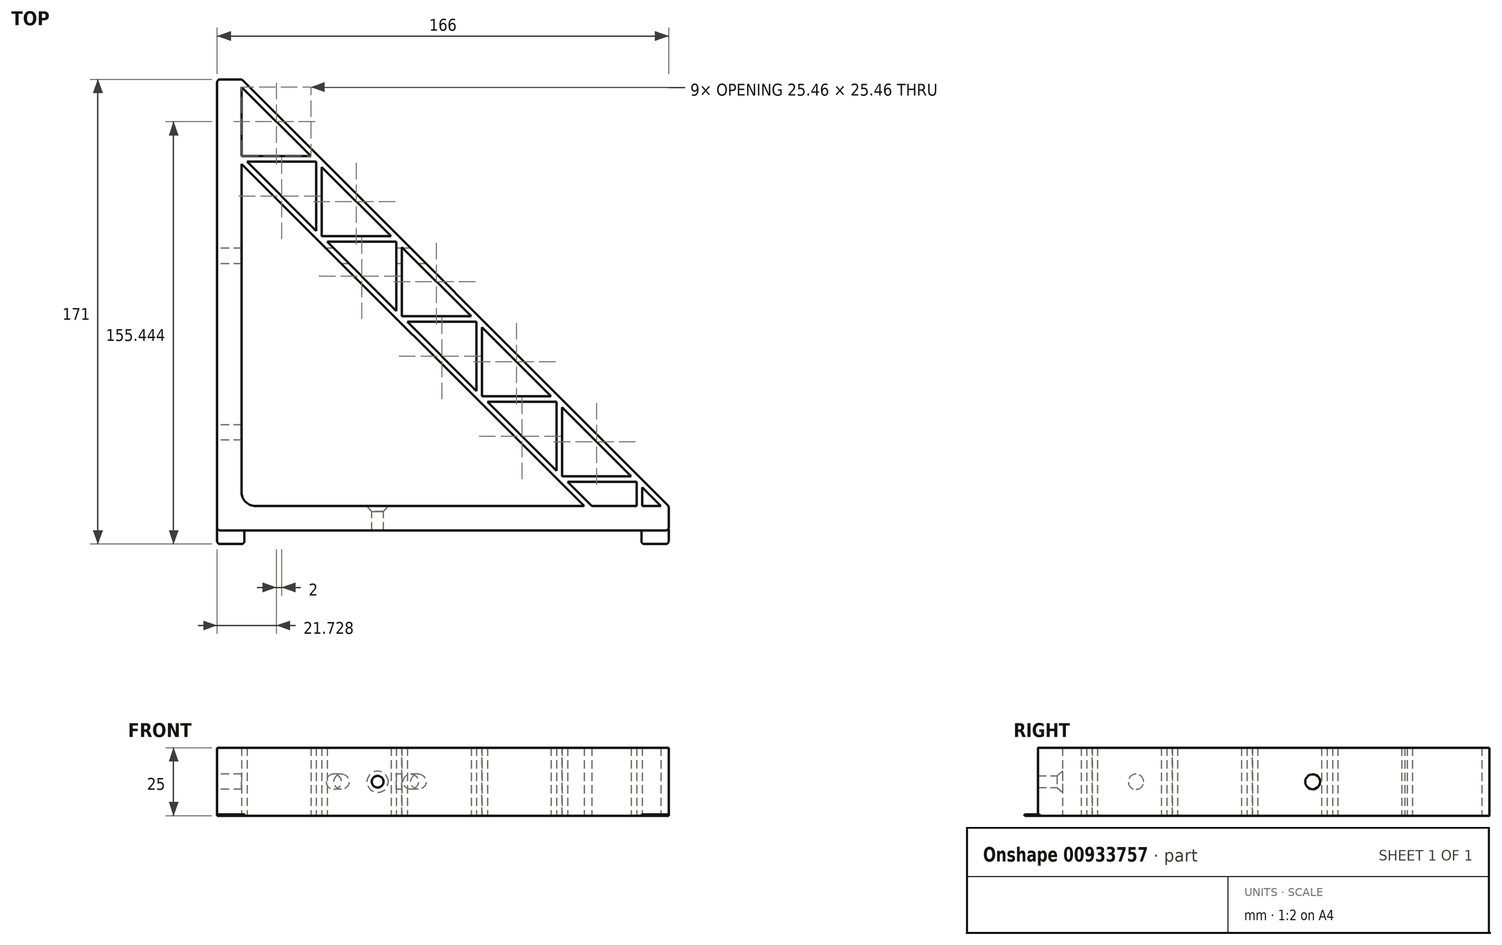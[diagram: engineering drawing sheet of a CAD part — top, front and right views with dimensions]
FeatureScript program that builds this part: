
annotation { "Feature Type Name" : "Feature", "Feature Type Description" : "" }
export const myFeature = defineFeature(function(context is Context, id is Id, definition is map)
    precondition{}
    {
        {
            var Q0;
            Q0=qCreatedBy(makeId("Top.planeOp"),FACE);
            var sketch = newSketch(context, id + "F0", { "sketchPlane" : qUnion([Q0])});
            skLineSegment(sketch, "E0", {"start": v(0, 0) * mm, "end": v(0, 175) * mm});
            skLineSegment(sketch, "E1", {"start": v(0, 175) * mm, "end": v(175, 0) * mm});
            skLineSegment(sketch, "E2", {"start": v(175, 0) * mm, "end": v(0, 0) * mm});
            skLineSegment(sketch, "E3", {"start": v(9, 134.89) * mm, "end": v(9, 9) * mm});
            skLineSegment(sketch, "E4", {"start": v(9, 9) * mm, "end": v(134.89, 9) * mm});
            skLineSegment(sketch, "E5", {"start": v(134.89, 9) * mm, "end": v(9, 134.89) * mm});
            skPoint(sketch, "E6", {"position": v(87.5, 87.5) * mm});
            skPoint(sketch, "E7", {"position": v(71.94, 71.94) * mm});
            skLineSegment(sketch, "E8", {"start": v(9, 163.17) * mm, "end": v(9, 137.72) * mm});
            skLineSegment(sketch, "E9", {"start": v(9, 137.72) * mm, "end": v(34.46, 137.72) * mm});
            skLineSegment(sketch, "E10", {"start": v(11, 135.72) * mm, "end": v(36.46, 135.72) * mm});
            skPoint(sketch, "E11", {"position": v(23.73, 135.72) * mm});
            skLineSegment(sketch, "E12", {"start": v(36.46, 135.72) * mm, "end": v(36.46, 110.26) * mm});
            skLineSegment(sketch, "E13", {"start": v(38.46, 108.26) * mm, "end": v(38.46, 133.72) * mm});
            skLineSegment(sketch, "E14", {"start": v(134.89, 9) * mm, "end": v(166, 9) * mm});
            skLineSegment(sketch, "E15", {"start": v(9, 134.89) * mm, "end": v(9, 138.17) * mm});
            skPoint(sketch, "E16", {"position": v(137.72, 9) * mm});
            skLineSegment(sketch, "E17", {"start": v(9, 137.72) * mm, "end": v(137.72, 9) * mm});
            skPoint(sketch, "E18", {"position": v(150.27, 21.9) * mm});
            skLineSegment(sketch, "E19", {"start": v(9, 163.17) * mm, "end": v(150.27, 21.9) * mm});
            skLineSegment(sketch, "E20", {"start": v(166, 9) * mm, "end": v(166, 0) * mm});
            skLineSegment(sketch, "E21", {"start": v(9, 163.17) * mm, "end": v(9, 166) * mm});
            skLineSegment(sketch, "E22", {"start": v(9, 166) * mm, "end": v(0, 166) * mm});
            skLineSegment(sketch, "E23.1.0.0", {"start": v(38.46, 108.26) * mm, "end": v(63.91, 108.26) * mm});
            skLineSegment(sketch, "E23.1.0.1", {"start": v(40.46, 106.26) * mm, "end": v(65.91, 106.26) * mm});
            skLineSegment(sketch, "E23.1.0.2", {"start": v(65.91, 106.26) * mm, "end": v(65.91, 80.8) * mm});
            skLineSegment(sketch, "E23.1.0.3", {"start": v(67.91, 78.8) * mm, "end": v(67.91, 104.26) * mm});
            skLineSegment(sketch, "E23.2.0.0", {"start": v(67.91, 78.8) * mm, "end": v(93.37, 78.8) * mm});
            skLineSegment(sketch, "E23.2.0.1", {"start": v(69.91, 76.8) * mm, "end": v(95.37, 76.8) * mm});
            skLineSegment(sketch, "E23.2.0.2", {"start": v(95.37, 76.8) * mm, "end": v(95.37, 51.35) * mm});
            skLineSegment(sketch, "E23.2.0.3", {"start": v(97.37, 49.35) * mm, "end": v(97.37, 74.8) * mm});
            skLineSegment(sketch, "E23.direction1", {"start": v(9, 137.72) * mm, "end": v(38.46, 108.26) * mm, "construction": true});
            skLineSegment(sketch, "E24.0.3.0", {"start": v(97.37, 49.35) * mm, "end": v(122.82, 49.35) * mm});
            skLineSegment(sketch, "E24.3.3.0", {"start": v(99.37, 47.35) * mm, "end": v(124.82, 47.35) * mm});
            skLineSegment(sketch, "E24.6.3.0", {"start": v(124.82, 47.35) * mm, "end": v(124.82, 21.9) * mm});
            skLineSegment(sketch, "E24.9.3.0", {"start": v(126.82, 19.9) * mm, "end": v(126.82, 45.35) * mm});
            skLineSegment(sketch, "E24.0.4.0", {"start": v(126.82, 19.9) * mm, "end": v(152.28, 19.9) * mm});
            skLineSegment(sketch, "E24.3.4.0", {"start": v(128.82, 17.9) * mm, "end": v(154.28, 17.9) * mm});
            skLineSegment(sketch, "E24.6.4.0", {"start": v(154.28, 17.9) * mm, "end": v(154.28, -7.56) * mm});
            skLineSegment(sketch, "E24.9.4.0", {"start": v(156.28, -9.56) * mm, "end": v(156.28, 15.9) * mm});
            skLineSegment(sketch, "E25", {"start": v(150.27, 21.9) * mm, "end": v(172.17, 0) * mm});
            skSolve(sketch);
        }
        {
            var Q0;
            Q0=makeQuery(id+"F0.imprint","IMPRINT",FACE,{"disambiguationData":[TD([[makeQuery(id+"F0.imprint","IMPRINT",EDGE,{"derivedFrom":sQuery(id+"F0.wireOp",EDGE,"E3")}),-1.0]])]});
            var Q1;
            {var subQ5=sQuery(id+"F0.wireOp",EDGE,"E8");Q1=makeQuery(id+"F0.imprint","IMPRINT",FACE,{"disambiguationData":[TD([[makeQuery(id+"F0.imprint","IMPRINT",EDGE,{"derivedFrom":subQ5}),-1.0]])]});}
            var Q2;
            {var subQ0=sQuery(id+"F0.wireOp",EDGE,"E9");Q2=makeQuery(id+"F0.imprint","IMPRINT",FACE,{"disambiguationData":[TD([[makeQuery(id+"F0.imprint","IMPRINT",EDGE,{"derivedFrom":subQ0}),-1.0]])]});}
            var Q3;
            {var subQ0=sQuery(id+"F0.wireOp",EDGE,"E12");Q3=makeQuery(id+"F0.imprint","IMPRINT",FACE,{"disambiguationData":[TD([[makeQuery(id+"F0.imprint","IMPRINT",EDGE,{"derivedFrom":subQ0}),1.0]])]});}
            var Q4;
            {var subQ0=sQuery(id+"F0.wireOp",EDGE,"t3oYEMUN-sFDN-Q4uO-rre0-XmO0z3MUqwwg");Q4=makeQuery(id+"F0.imprint","IMPRINT",FACE,{"disambiguationData":[TD([[makeQuery(id+"F0.imprint","IMPRINT",EDGE,{"derivedFrom":subQ0}),-1.0]])]});}
            var Q5;
            {var subQ0=sQuery(id+"F0.wireOp",EDGE,"Gh5ZCY8b-JTnj-C4Vn-PBZv-iaPauiYJcpUC");Q5=makeQuery(id+"F0.imprint","IMPRINT",FACE,{"disambiguationData":[TD([[makeQuery(id+"F0.imprint","IMPRINT",EDGE,{"derivedFrom":subQ0}),1.0]])]});}
            var Q6;
            {var subQ0=sQuery(id+"F0.wireOp",EDGE,"uzZHcgCa-ZNne-41at-UcpQ-2XL1grKBjjWO");Q6=makeQuery(id+"F0.imprint","IMPRINT",FACE,{"disambiguationData":[TD([[makeQuery(id+"F0.imprint","IMPRINT",EDGE,{"derivedFrom":subQ0}),-1.0]])]});}
            var Q7;
            {var subQ0=sQuery(id+"F0.wireOp",EDGE,"vpBYavAs-v1ow-tuZv-KXIh-prGS5gAtpX7B");Q7=makeQuery(id+"F0.imprint","IMPRINT",FACE,{"disambiguationData":[TD([[makeQuery(id+"F0.imprint","IMPRINT",EDGE,{"derivedFrom":subQ0}),1.0]])]});}
            var Q8;
            {var subQ0=sQuery(id+"F0.wireOp",EDGE,"fNY8aZDA-NZx5-W13j-vITE-4YfcdmMxDZ5e");Q8=makeQuery(id+"F0.imprint","IMPRINT",FACE,{"disambiguationData":[TD([[makeQuery(id+"F0.imprint","IMPRINT",EDGE,{"derivedFrom":subQ0}),-1.0]])]});}
            var Q9;
            {var subQ0=sQuery(id+"F0.wireOp",EDGE,"PBqfKtz1-XXqo-IEwp-yejb-xkakkozYTLbb");Q9=makeQuery(id+"F0.imprint","IMPRINT",FACE,{"disambiguationData":[TD([[makeQuery(id+"F0.imprint","IMPRINT",EDGE,{"derivedFrom":subQ0}),1.0]])]});}
            var Q10;
            {var subQ0=sQuery(id+"F0.wireOp",EDGE,"PBqfKtz1-XXqo-IEwp-yejb-xkakkozYTLbb");var subQ1=sQuery(id+"F0.wireOp",EDGE,"0tnvtRqo-Ka0R-me24-QFtn-nfTgzuCr438E");var subQ2=makeQuery(id+"F0.imprint","INTERSECT",VERTEX,{"derivedFrom":[subQ1,subQ0]});Q10=makeQuery(id+"F0.imprint","IMPRINT",FACE,{"disambiguationData":[TD([[makeQuery(id+"F0.imprint","IMPRINT",EDGE,{"disambiguationData":[TD([[subQ2,1.0]])],"derivedFrom":subQ1}),1.0]])]});}
            var Q11;
            {var subQ1=sQuery(id+"F0.wireOp",EDGE,"TcHh0TCD-bz2r-2cmx-PJUQ-hrZb60m40xgq");var subQ5=sQuery(id+"F0.wireOp",EDGE,"0tnvtRqo-Ka0R-me24-QFtn-nfTgzuCr438E");var subQ6=makeQuery(id+"F0.imprint","INTERSECT",VERTEX,{"derivedFrom":[subQ5,subQ1]});Q11=makeQuery(id+"F0.imprint","IMPRINT",FACE,{"disambiguationData":[TD([[makeQuery(id+"F0.imprint","IMPRINT",EDGE,{"disambiguationData":[TD([[subQ6,1.0]])],"derivedFrom":subQ5}),1.0]])]});}
            var Q12;
            {var subQ0=sQuery(id+"F0.wireOp",EDGE,"TcHh0TCD-bz2r-2cmx-PJUQ-hrZb60m40xgq");var subQ1=sQuery(id+"F0.wireOp",EDGE,"p0dbSUAr-ZKRw-19DJ-W5tp-fSP5nnLVepNG");var subQ2=makeQuery(id+"F0.imprint","INTERSECT",VERTEX,{"derivedFrom":[subQ1,subQ0]});Q12=makeQuery(id+"F0.imprint","IMPRINT",FACE,{"disambiguationData":[TD([[makeQuery(id+"F0.imprint","IMPRINT",EDGE,{"disambiguationData":[TD([[subQ2,-1.0]])],"derivedFrom":subQ1}),1.0]])]});}
            var Q13;
            {var subQ0=sQuery(id+"F0.wireOp",EDGE,"E10");var subQ1=sQuery(id+"F0.wireOp",EDGE,"0tnvtRqo-Ka0R-me24-QFtn-nfTgzuCr438E");var subQ2=makeQuery(id+"F0.imprint","INTERSECT",VERTEX,{"derivedFrom":[subQ1,subQ0]});Q13=makeQuery(id+"F0.imprint","IMPRINT",FACE,{"disambiguationData":[TD([[makeQuery(id+"F0.imprint","IMPRINT",EDGE,{"disambiguationData":[TD([[subQ2,-1.0]])],"derivedFrom":subQ1}),1.0]])]});}
            var Q14;
            {var subQ11=sQuery(id+"F0.wireOp",EDGE,"E5");Q14=makeQuery(id+"F0.imprint","IMPRINT",FACE,{"disambiguationData":[TD([[makeQuery(id+"F0.imprint","IMPRINT",EDGE,{"derivedFrom":subQ11}),-1.0]])]});}
            var Q15;
            {var subQ0=sQuery(id+"F0.wireOp",EDGE,"3CZCHI8V-pq78-QH3n-k3AF-cjWYhrhBDTe4");Q15=makeQuery(id+"F0.imprint","IMPRINT",FACE,{"disambiguationData":[TD([[makeQuery(id+"F0.imprint","IMPRINT",EDGE,{"derivedFrom":subQ0}),-1.0]])]});}
            var Q16;
            {var subQ7=sQuery(id+"F0.wireOp",EDGE,"E21");Q16=makeQuery(id+"F0.imprint","IMPRINT",FACE,{"disambiguationData":[TD([[makeQuery(id+"F0.imprint","IMPRINT",EDGE,{"derivedFrom":subQ7}),-1.0]])]});}
            var Q17;
            {var subQ0=sQuery(id+"F0.wireOp",EDGE,"E23.1.0.0");Q17=makeQuery(id+"F0.imprint","IMPRINT",FACE,{"disambiguationData":[TD([[makeQuery(id+"F0.imprint","IMPRINT",EDGE,{"derivedFrom":subQ0}),-1.0]])]});}
            var Q18;
            {var subQ0=sQuery(id+"F0.wireOp",EDGE,"E23.1.0.2");Q18=makeQuery(id+"F0.imprint","IMPRINT",FACE,{"disambiguationData":[TD([[makeQuery(id+"F0.imprint","IMPRINT",EDGE,{"derivedFrom":subQ0}),1.0]])]});}
            var Q19;
            {var subQ0=sQuery(id+"F0.wireOp",EDGE,"E23.2.0.0");Q19=makeQuery(id+"F0.imprint","IMPRINT",FACE,{"disambiguationData":[TD([[makeQuery(id+"F0.imprint","IMPRINT",EDGE,{"derivedFrom":subQ0}),-1.0]])]});}
            var Q20;
            {var subQ0=sQuery(id+"F0.wireOp",EDGE,"E23.2.0.2");Q20=makeQuery(id+"F0.imprint","IMPRINT",FACE,{"disambiguationData":[TD([[makeQuery(id+"F0.imprint","IMPRINT",EDGE,{"derivedFrom":subQ0}),1.0]])]});}
            var Q21;
            {var subQ0=sQuery(id+"F0.wireOp",EDGE,"E24.0.3.0");Q21=makeQuery(id+"F0.imprint","IMPRINT",FACE,{"disambiguationData":[TD([[makeQuery(id+"F0.imprint","IMPRINT",EDGE,{"derivedFrom":subQ0}),-1.0]])]});}
            var Q22;
            {var subQ0=sQuery(id+"F0.wireOp",EDGE,"E24.6.3.0");Q22=makeQuery(id+"F0.imprint","IMPRINT",FACE,{"disambiguationData":[TD([[makeQuery(id+"F0.imprint","IMPRINT",EDGE,{"derivedFrom":subQ0}),1.0]])]});}
            var Q23;
            {var subQ0=sQuery(id+"F0.wireOp",EDGE,"E24.0.4.0");Q23=makeQuery(id+"F0.imprint","IMPRINT",FACE,{"disambiguationData":[TD([[makeQuery(id+"F0.imprint","IMPRINT",EDGE,{"derivedFrom":subQ0}),-1.0]])]});}
            var Q24;
            {var subQ0=sQuery(id+"F0.wireOp",EDGE,"E24.6.4.0");var subQ1=sQuery(id+"F0.wireOp",EDGE,"E14");var subQ2=makeQuery(id+"F0.imprint","INTERSECT",VERTEX,{"derivedFrom":[subQ1,subQ0]});Q24=makeQuery(id+"F0.imprint","IMPRINT",FACE,{"disambiguationData":[TD([[makeQuery(id+"F0.imprint","IMPRINT",EDGE,{"disambiguationData":[TD([[subQ2,-1.0]])],"derivedFrom":subQ1}),1.0]])]});}
            var Q25;
            {var subQ0=sQuery(id+"F0.wireOp",EDGE,"E24.9.4.0");var subQ1=sQuery(id+"F0.wireOp",EDGE,"E2");var subQ2=makeQuery(id+"F0.imprint","INTERSECT",VERTEX,{"derivedFrom":[subQ1,subQ0]});Q25=makeQuery(id+"F0.imprint","IMPRINT",FACE,{"disambiguationData":[TD([[makeQuery(id+"F0.imprint","IMPRINT",EDGE,{"disambiguationData":[TD([[subQ2,-1.0]])],"derivedFrom":subQ1}),-1.0]])]});}
            var Q26;
            {var subQ0=sQuery(id+"F0.wireOp",EDGE,"E20");var subQ1=sQuery(id+"F0.wireOp",EDGE,"E2");var subQ2=makeQuery(id+"F0.imprint","INTERSECT",VERTEX,{"derivedFrom":[subQ1,subQ0]});Q26=makeQuery(id+"F0.imprint","IMPRINT",FACE,{"disambiguationData":[TD([[makeQuery(id+"F0.imprint","IMPRINT",EDGE,{"disambiguationData":[TD([[subQ2,-1.0]])],"derivedFrom":subQ1}),-1.0]])]});}
            var Q27;
            {var subQ1=sQuery(id+"F0.wireOp",EDGE,"E14");var subQ3=sQuery(id+"F0.wireOp",EDGE,"E25");var subQ4=makeQuery(id+"F0.imprint","INTERSECT",VERTEX,{"derivedFrom":[subQ1,subQ3]});Q27=makeQuery(id+"F0.imprint","IMPRINT",FACE,{"disambiguationData":[TD([[makeQuery(id+"F0.imprint","IMPRINT",EDGE,{"disambiguationData":[TD([[subQ4,-1.0]])],"derivedFrom":subQ3}),1.0]])]});}
            extrude(context, id + "F1", {"entities" : qUnion([Q0, Q1, Q2, Q3, Q4, Q5, Q6, Q7, Q8, Q9, Q10, Q11, Q12, Q13, Q14, Q15, Q16, Q17, Q18, Q19, Q20, Q21, Q22, Q23, Q24, Q25, Q26, Q27]), "depth" : 25 * mm, "offsetDistance" : 25 * mm});
        }
        {
            var Q0;
            Q0=makeQuery(id+"F1.opExtrude","SWEPT_FACE",FACE,{"disambiguationData":[OSD([sQuery(id+"F0.wireOp",EDGE,"E0")])]});
            var sketch = newSketch(context, id + "F2", { "sketchPlane" : qUnion([Q0])});
            skLineSegment(sketch, "E26", {"start": v(0, 12.5) * mm, "end": v(-166, 12.5) * mm, "construction": true});
            skLineSegment(sketch, "E27", {"start": v(-9, 25) * mm, "end": v(-9, 0) * mm, "construction": true});
            skPoint(sketch, "E28", {"position": v(-9, 12.5) * mm});
            skPoint(sketch, "E29", {"position": v(-36, 12.5) * mm});
            skPoint(sketch, "E30", {"position": v(-86, 12.5) * mm});
            skSolve(sketch);
        }
        {
            var Q0;
            Q0=sQuery(id+"F2.wireOp",VERTEX,"E29");
            var Q1;
            Q1=makeQuery(id+"F1.opExtrude","SWEPT_BODY",BODY,{"disambiguationData":[OSD([sQuery(id+"F0.wireOp",EDGE,"E0"),sQuery(id+"F0.wireOp",EDGE,"E1"),sQuery(id+"F0.wireOp",EDGE,"E2"),sQuery(id+"F0.wireOp",EDGE,"E3"),sQuery(id+"F0.wireOp",EDGE,"E4"),sQuery(id+"F0.wireOp",EDGE,"E5"),sQuery(id+"F0.wireOp",EDGE,"E9"),sQuery(id+"F0.wireOp",EDGE,"E10"),sQuery(id+"F0.wireOp",EDGE,"E12"),sQuery(id+"F0.wireOp",EDGE,"E13"),sQuery(id+"F0.wireOp",EDGE,"t3oYEMUN-sFDN-Q4uO-rre0-XmO0z3MUqwwg"),sQuery(id+"F0.wireOp",EDGE,"wbD9qHZu-pqNc-cMZF-pwQb-4rQk1D1zuLdl"),sQuery(id+"F0.wireOp",EDGE,"Gh5ZCY8b-JTnj-C4Vn-PBZv-iaPauiYJcpUC"),sQuery(id+"F0.wireOp",EDGE,"IqIC1HOr-2qrz-Gsiv-DJaI-mmAGYpswksB0"),sQuery(id+"F0.wireOp",EDGE,"uzZHcgCa-ZNne-41at-UcpQ-2XL1grKBjjWO"),sQuery(id+"F0.wireOp",EDGE,"U4Ez3DGl-Xapn-CNsW-HCYy-rBAmkq0lTpTK"),sQuery(id+"F0.wireOp",EDGE,"vpBYavAs-v1ow-tuZv-KXIh-prGS5gAtpX7B"),sQuery(id+"F0.wireOp",EDGE,"AZhl3Uul-uOOh-n7bd-IfFj-a6V9GQ91CMK2"),sQuery(id+"F0.wireOp",EDGE,"fNY8aZDA-NZx5-W13j-vITE-4YfcdmMxDZ5e"),sQuery(id+"F0.wireOp",EDGE,"W6oHj5A9-C86R-qUiH-kgSU-SLB568lxmBaT"),sQuery(id+"F0.wireOp",EDGE,"3CZCHI8V-pq78-QH3n-k3AF-cjWYhrhBDTe4"),sQuery(id+"F0.wireOp",EDGE,"E14"),sQuery(id+"F0.wireOp",EDGE,"E15"),sQuery(id+"F0.wireOp",EDGE,"rwknU0Rr-BnYf-MzcB-lmkz-0eZFg8cNU43Z"),sQuery(id+"F0.wireOp",EDGE,"E17"),sQuery(id+"F0.wireOp",EDGE,"E19")])]});
            hole(context, id + "F3", {"style" : HoleStyle.SIMPLE, "endStyle" : HoleEndStyle.BLIND, "standardTappedOrClearance" : lookupTablePath({ "fit" : "Normal (ASME)", "standard" : "ANSI", "size" : "#10", "type" : "Clearance" }), "standardBlindInLast" : lookupTablePath({ "fit" : "Normal", "standard" : "ANSI", "engagement" : "75%", "pitch" : "24 tpi", "size" : "#10", "type" : "Clearance & tapped" }), "holeDiameter" : 5.61 * mm, "majorDiameter" : 5 * mm, "holeDepth" : 25 * mm, "isTappedThrough" : true, "tappedDepth" : 12 * mm, "tapClearance" : 3, "locations" : qUnion([Q0]), "scope" : qUnion([Q1])});
        }
        {
            var Q0;
            Q0=makeQuery(id+"F1.opExtrude","SWEPT_FACE",FACE,{"disambiguationData":[OSD([sQuery(id+"F0.wireOp",EDGE,"E0")])]});
            var sketch = newSketch(context, id + "F4", { "sketchPlane" : qUnion([Q0])});
            skLineSegment(sketch, "E31", {"start": v(0, 12.5) * mm, "end": v(-166, 12.5) * mm, "construction": true});
            skPoint(sketch, "E32", {"position": v(-36, 12.5) * mm});
            skPoint(sketch, "E33", {"position": v(-101, 12.5) * mm});
            skSolve(sketch);
        }
        {
            var Q0;
            Q0=sQuery(id+"F4.wireOp",VERTEX,"E33");
            var Q1;
            Q1=makeQuery(id+"F1.opExtrude","SWEPT_BODY",BODY,{"disambiguationData":[OSD([sQuery(id+"F0.wireOp",EDGE,"E0"),sQuery(id+"F0.wireOp",EDGE,"E1"),sQuery(id+"F0.wireOp",EDGE,"E2"),sQuery(id+"F0.wireOp",EDGE,"E3"),sQuery(id+"F0.wireOp",EDGE,"E4"),sQuery(id+"F0.wireOp",EDGE,"E5"),sQuery(id+"F0.wireOp",EDGE,"E9"),sQuery(id+"F0.wireOp",EDGE,"E10"),sQuery(id+"F0.wireOp",EDGE,"E12"),sQuery(id+"F0.wireOp",EDGE,"E13"),sQuery(id+"F0.wireOp",EDGE,"t3oYEMUN-sFDN-Q4uO-rre0-XmO0z3MUqwwg"),sQuery(id+"F0.wireOp",EDGE,"wbD9qHZu-pqNc-cMZF-pwQb-4rQk1D1zuLdl"),sQuery(id+"F0.wireOp",EDGE,"Gh5ZCY8b-JTnj-C4Vn-PBZv-iaPauiYJcpUC"),sQuery(id+"F0.wireOp",EDGE,"IqIC1HOr-2qrz-Gsiv-DJaI-mmAGYpswksB0"),sQuery(id+"F0.wireOp",EDGE,"uzZHcgCa-ZNne-41at-UcpQ-2XL1grKBjjWO"),sQuery(id+"F0.wireOp",EDGE,"U4Ez3DGl-Xapn-CNsW-HCYy-rBAmkq0lTpTK"),sQuery(id+"F0.wireOp",EDGE,"vpBYavAs-v1ow-tuZv-KXIh-prGS5gAtpX7B"),sQuery(id+"F0.wireOp",EDGE,"AZhl3Uul-uOOh-n7bd-IfFj-a6V9GQ91CMK2"),sQuery(id+"F0.wireOp",EDGE,"fNY8aZDA-NZx5-W13j-vITE-4YfcdmMxDZ5e"),sQuery(id+"F0.wireOp",EDGE,"W6oHj5A9-C86R-qUiH-kgSU-SLB568lxmBaT"),sQuery(id+"F0.wireOp",EDGE,"3CZCHI8V-pq78-QH3n-k3AF-cjWYhrhBDTe4"),sQuery(id+"F0.wireOp",EDGE,"E14"),sQuery(id+"F0.wireOp",EDGE,"E15"),sQuery(id+"F0.wireOp",EDGE,"rwknU0Rr-BnYf-MzcB-lmkz-0eZFg8cNU43Z"),sQuery(id+"F0.wireOp",EDGE,"E17"),sQuery(id+"F0.wireOp",EDGE,"E19")])]});
            hole(context, id + "F5", {"style" : HoleStyle.SIMPLE, "endStyle" : HoleEndStyle.BLIND, "standardTappedOrClearance" : lookupTablePath({ "fit" : "Normal (ASME)", "standard" : "ANSI", "size" : "#10", "type" : "Clearance" }), "standardBlindInLast" : lookupTablePath({ "fit" : "Normal", "standard" : "ANSI", "engagement" : "75%", "pitch" : "24 tpi", "size" : "#10", "type" : "Clearance & tapped" }), "holeDiameter" : 5.61 * mm, "majorDiameter" : 5 * mm, "holeDepth" : 85 * mm, "isTappedThrough" : true, "tappedDepth" : 12 * mm, "tapClearance" : 3, "locations" : qUnion([Q0]), "scope" : qUnion([Q1])});
        }
        {
            var Q0;
            Q0=makeQuery(id+"F1.opExtrude","SWEPT_FACE",FACE,{"disambiguationData":[OSD([sQuery(id+"F0.wireOp",EDGE,"E4")])]});
            var sketch = newSketch(context, id + "F6", { "sketchPlane" : qUnion([Q0])});
            skLineSegment(sketch, "E34", {"start": v(-9, 12.5) * mm, "end": v(-59.86, 12.5) * mm, "construction": true});
            skPoint(sketch, "E35", {"position": v(-59, 12.5) * mm});
            skSolve(sketch);
        }
        {
            var Q0;
            Q0=sQuery(id+"F6.wireOp",VERTEX,"E35");
            var Q1;
            Q1=makeQuery(id+"F1.opExtrude","SWEPT_BODY",BODY,{"disambiguationData":[OSD([sQuery(id+"F0.wireOp",EDGE,"E0"),sQuery(id+"F0.wireOp",EDGE,"E1"),sQuery(id+"F0.wireOp",EDGE,"E2"),sQuery(id+"F0.wireOp",EDGE,"E3"),sQuery(id+"F0.wireOp",EDGE,"E4"),sQuery(id+"F0.wireOp",EDGE,"E5"),sQuery(id+"F0.wireOp",EDGE,"E9"),sQuery(id+"F0.wireOp",EDGE,"E10"),sQuery(id+"F0.wireOp",EDGE,"E12"),sQuery(id+"F0.wireOp",EDGE,"E13"),sQuery(id+"F0.wireOp",EDGE,"t3oYEMUN-sFDN-Q4uO-rre0-XmO0z3MUqwwg"),sQuery(id+"F0.wireOp",EDGE,"wbD9qHZu-pqNc-cMZF-pwQb-4rQk1D1zuLdl"),sQuery(id+"F0.wireOp",EDGE,"Gh5ZCY8b-JTnj-C4Vn-PBZv-iaPauiYJcpUC"),sQuery(id+"F0.wireOp",EDGE,"IqIC1HOr-2qrz-Gsiv-DJaI-mmAGYpswksB0"),sQuery(id+"F0.wireOp",EDGE,"uzZHcgCa-ZNne-41at-UcpQ-2XL1grKBjjWO"),sQuery(id+"F0.wireOp",EDGE,"U4Ez3DGl-Xapn-CNsW-HCYy-rBAmkq0lTpTK"),sQuery(id+"F0.wireOp",EDGE,"vpBYavAs-v1ow-tuZv-KXIh-prGS5gAtpX7B"),sQuery(id+"F0.wireOp",EDGE,"AZhl3Uul-uOOh-n7bd-IfFj-a6V9GQ91CMK2"),sQuery(id+"F0.wireOp",EDGE,"fNY8aZDA-NZx5-W13j-vITE-4YfcdmMxDZ5e"),sQuery(id+"F0.wireOp",EDGE,"W6oHj5A9-C86R-qUiH-kgSU-SLB568lxmBaT"),sQuery(id+"F0.wireOp",EDGE,"3CZCHI8V-pq78-QH3n-k3AF-cjWYhrhBDTe4"),sQuery(id+"F0.wireOp",EDGE,"E14"),sQuery(id+"F0.wireOp",EDGE,"E15"),sQuery(id+"F0.wireOp",EDGE,"rwknU0Rr-BnYf-MzcB-lmkz-0eZFg8cNU43Z"),sQuery(id+"F0.wireOp",EDGE,"E17"),sQuery(id+"F0.wireOp",EDGE,"E19")])]});
            hole(context, id + "F7", {"style" : HoleStyle.C_SINK, "endStyle" : HoleEndStyle.BLIND, "standardTappedOrClearance" : lookupTablePath({ "fit" : "Normal (ASME)", "standard" : "ANSI", "size" : "#6", "type" : "Clearance" }), "standardBlindInLast" : lookupTablePath({ "fit" : "Normal", "standard" : "ANSI", "engagement" : "75%", "pitch" : "32 tpi", "size" : "#6", "type" : "Clearance & tapped" }), "holeDiameter" : 4.32 * mm, "cSinkDiameter" : 7.8 * mm, "cSinkAngle" : 82 * degree, "majorDiameter" : 5 * mm, "holeDepth" : 25 * mm, "isTappedThrough" : true, "tappedDepth" : 12 * mm, "tapClearance" : 3, "locations" : qUnion([Q0]), "scope" : qUnion([Q1])});
        }
        {
            var Q0;
            Q0=makeQuery(id+"F1.opExtrude","SWEPT_EDGE",EDGE,{"disambiguationData":[OSD([sQuery(id+"F0.wireOp",EDGE,"E3"),sQuery(id+"F0.wireOp",EDGE,"E4")])]});
            fillet(context, id + "F8", {"entities" : qUnion([Q0]), "radius" : 5 * mm, "tangentPropagation" : true, "allowEdgeOverflow" : false});
        }
        {
            var Q0;
            Q0=makeQuery(id+"F1.opExtrude","SWEPT_EDGE",EDGE,{"disambiguationData":[OSD([sQuery(id+"F0.wireOp",EDGE,"E1"),sQuery(id+"F0.wireOp",EDGE,"E14"),sQuery(id+"F0.wireOp",EDGE,"E20")])]});
            var Q1;
            Q1=makeQuery(id+"F1.opExtrude","SWEPT_EDGE",EDGE,{"disambiguationData":[OSD([sQuery(id+"F0.wireOp",EDGE,"E2"),sQuery(id+"F0.wireOp",EDGE,"E20")])]});
            var Q2;
            Q2=makeQuery(id+"F1.opExtrude","SWEPT_EDGE",EDGE,{"disambiguationData":[OSD([sQuery(id+"F0.wireOp",EDGE,"E0"),sQuery(id+"F0.wireOp",EDGE,"E2")])]});
            var Q3;
            Q3=makeQuery(id+"F1.opExtrude","SWEPT_EDGE",EDGE,{"disambiguationData":[OSD([sQuery(id+"F0.wireOp",EDGE,"E0"),sQuery(id+"F0.wireOp",EDGE,"E22")])]});
            var Q4;
            Q4=makeQuery(id+"F1.opExtrude","SWEPT_EDGE",EDGE,{"disambiguationData":[OSD([sQuery(id+"F0.wireOp",EDGE,"E1"),sQuery(id+"F0.wireOp",EDGE,"E21"),sQuery(id+"F0.wireOp",EDGE,"E22")])]});
            fillet(context, id + "F9", {"entities" : qUnion([Q0, Q1, Q2, Q3, Q4]), "radius" : 1 * mm, "tangentPropagation" : true, "allowEdgeOverflow" : false});
        }
        {
            var Q0;
            Q0=makeQuery(id+"F1.opExtrude","CAP_FACE",FACE,{"disambiguationData":[OSD([sQuery(id+"F0.wireOp",EDGE,"E0"),sQuery(id+"F0.wireOp",EDGE,"E1"),sQuery(id+"F0.wireOp",EDGE,"E2"),sQuery(id+"F0.wireOp",EDGE,"E3"),sQuery(id+"F0.wireOp",EDGE,"E4"),sQuery(id+"F0.wireOp",EDGE,"E5"),sQuery(id+"F0.wireOp",EDGE,"E8"),sQuery(id+"F0.wireOp",EDGE,"E9"),sQuery(id+"F0.wireOp",EDGE,"E10"),sQuery(id+"F0.wireOp",EDGE,"E12"),sQuery(id+"F0.wireOp",EDGE,"E13"),sQuery(id+"F0.wireOp",EDGE,"E14"),sQuery(id+"F0.wireOp",EDGE,"E15"),sQuery(id+"F0.wireOp",EDGE,"E17"),sQuery(id+"F0.wireOp",EDGE,"E19"),sQuery(id+"F0.wireOp",EDGE,"E20"),sQuery(id+"F0.wireOp",EDGE,"E22"),sQuery(id+"F0.wireOp",EDGE,"E23.1.0.0"),sQuery(id+"F0.wireOp",EDGE,"E23.1.0.1"),sQuery(id+"F0.wireOp",EDGE,"E23.1.0.2"),sQuery(id+"F0.wireOp",EDGE,"E23.1.0.3"),sQuery(id+"F0.wireOp",EDGE,"E23.2.0.0"),sQuery(id+"F0.wireOp",EDGE,"E23.2.0.1"),sQuery(id+"F0.wireOp",EDGE,"E23.2.0.2"),sQuery(id+"F0.wireOp",EDGE,"E23.2.0.3"),sQuery(id+"F0.wireOp",EDGE,"E24.0.3.0"),sQuery(id+"F0.wireOp",EDGE,"E24.3.3.0"),sQuery(id+"F0.wireOp",EDGE,"E24.6.3.0"),sQuery(id+"F0.wireOp",EDGE,"E24.9.3.0"),sQuery(id+"F0.wireOp",EDGE,"E24.0.4.0"),sQuery(id+"F0.wireOp",EDGE,"E24.3.4.0"),sQuery(id+"F0.wireOp",EDGE,"E24.6.4.0"),sQuery(id+"F0.wireOp",EDGE,"E24.9.4.0"),sQuery(id+"F0.wireOp",EDGE,"E25")])],"isStart":true});
            var sketch = newSketch(context, id + "F10", { "sketchPlane" : qUnion([Q0])});
            skLineSegment(sketch, "E36.bottom", {"start": v(0, -1.43) * mm, "end": v(10, -1.43) * mm});
            skLineSegment(sketch, "E36.top", {"start": v(0, 5) * mm, "end": v(10, 5) * mm});
            skLineSegment(sketch, "E36.left", {"start": v(0, -1.43) * mm, "end": v(0, 5) * mm});
            skLineSegment(sketch, "E36.right", {"start": v(10, -1.43) * mm, "end": v(10, 5) * mm});
            skLineSegment(sketch, "E37.bottom", {"start": v(166, -0.53) * mm, "end": v(156, -0.53) * mm});
            skLineSegment(sketch, "E37.top", {"start": v(166, 5) * mm, "end": v(156, 5) * mm});
            skLineSegment(sketch, "E37.left", {"start": v(166, -0.53) * mm, "end": v(166, 5) * mm});
            skLineSegment(sketch, "E37.right", {"start": v(156, -0.53) * mm, "end": v(156, 5) * mm});
            skSolve(sketch);
        }
        {
            var Q0;
            {var subQ1=sQuery(id+"F10.wireOp",EDGE,"E37.top");Q0=makeQuery(id+"F10.imprint","IMPRINT",FACE,{"disambiguationData":[TD([[makeQuery(id+"F10.imprint","IMPRINT",EDGE,{"derivedFrom":subQ1}),1.0]])]});}
            var Q1;
            {var subQ4=sQuery(id+"F10.wireOp",EDGE,"E36.top");Q1=makeQuery(id+"F10.imprint","IMPRINT",FACE,{"disambiguationData":[TD([[makeQuery(id+"F10.imprint","IMPRINT",EDGE,{"derivedFrom":subQ4}),-1.0]])]});}
            extrude(context, id + "F11", {"entities" : qUnion([Q0, Q1]), "operationType" : NewBodyOperationType.ADD, "depth" : -.4 * mm, "offsetDistance" : 25 * mm});
        }
        {
            var Q0;
            Q0=makeQuery(id+"F11.opExtrude","SWEPT_EDGE",EDGE,{"disambiguationData":[OSD([sQuery(id+"F10.wireOp",EDGE,"E37.top"),sQuery(id+"F10.wireOp",EDGE,"E37.left")])]});
            var Q1;
            Q1=makeQuery(id+"F11.opExtrude","SWEPT_EDGE",EDGE,{"disambiguationData":[OSD([sQuery(id+"F10.wireOp",EDGE,"E37.top"),sQuery(id+"F10.wireOp",EDGE,"E37.right")])]});
            var Q2;
            Q2=makeQuery(id+"F11.opExtrude","SWEPT_EDGE",EDGE,{"disambiguationData":[OSD([sQuery(id+"F10.wireOp",EDGE,"E36.top"),sQuery(id+"F10.wireOp",EDGE,"E36.left")])]});
            var Q3;
            Q3=makeQuery(id+"F11.opExtrude","SWEPT_EDGE",EDGE,{"disambiguationData":[OSD([sQuery(id+"F10.wireOp",EDGE,"E36.top"),sQuery(id+"F10.wireOp",EDGE,"E36.right")])]});
            fillet(context, id + "F12", {"entities" : qUnion([Q0, Q1, Q2, Q3]), "radius" : 1 * mm, "tangentPropagation" : true, "allowEdgeOverflow" : false});
        }
    });
